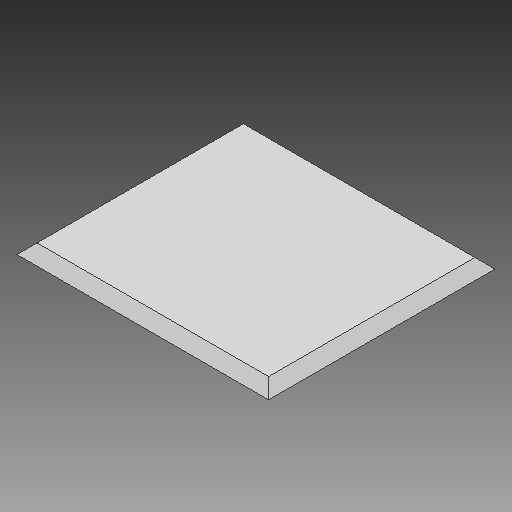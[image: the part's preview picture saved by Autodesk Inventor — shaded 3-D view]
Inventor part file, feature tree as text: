
AUTODESK INVENTOR PART (.ipt)
format: ipt  version: 2018 (Build 220112000, 112)  size: 78,336 bytes
history: native  units: mm
features: other x3, sketch x1
ambient origin geometry x8: Origin, YZ Plane, XZ Plane, XY Plane, X Axis, Y Axis, Z Axis, Center Point
bodies: Volumenkörper1 (feature_tree)
feature tree (4):
  other  "Wand1.ipt"
  other  "Volumenkörper1::Wand1.ipt"
  other  "Bezeichnung1"
  sketch  "Skizze1"  dims[d0=10.0mm]
